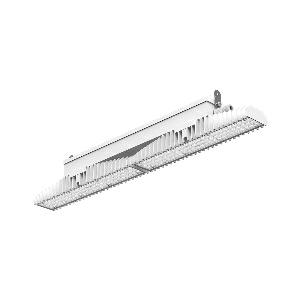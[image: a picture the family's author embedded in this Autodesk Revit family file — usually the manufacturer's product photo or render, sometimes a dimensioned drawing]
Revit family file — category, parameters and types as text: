
# Revit family: 3f_filippi_-_3f_lem_ampio_3f_filippi_-_59161_-_3f_lem_1_1_led_100-865_cr_ampio_7060
name_source: partatom
category: Lighting Fixtures
units: mm (PartAtom-declared; Revit-internal decimal feet)

## family parameters
Cut with Voids When Loaded = No
Host = Face
Light Source = No
Part Type = Normal
Room Calculation Point = No
Round Connector Dimension = Use Diameter
Shared = No

## types (1)
- 3F Filippi - 3F LEM Ampio (1 x LED, 16989 lm, 109 W, 6500 K)
    Apparent Load = 109 VA
    Approval mark = CE
    CIE Flux Codes = 60 92 99 100 100
    Color Rendering = 80
    Color Temperature = 6500 K
    Control Gear = Electronic ballast
    Default Elevation = 1800 mm
    Description = Industrial luminaire with high light output and high luminous efficiency designed with the most innovative technologies for environments with temperature up to 55°C.

ILLUMINOTECHNICAL
Luminous efficiency 100% (DLOR 100%, ULOR 0%).
Initial luminous flux of the luminaire 16989 lm.
Direct symmetric wide distribution: the illuminated area has a rectangular shape.
Installation Interdistance Transv.D = 1.58 x hu - Long.D = 1.45 x hu.
Tabular UGR (CIE 117 - 4H-8H; S=0.25H; 70/50/20): RUG 26.3 - 27.3.
Beam angle: 93° - 99°.
Luminous efficacy 156 lm/W.
Lifetime (L93/B10): 30000 h. (tq+25°C)
Lifetime (L90/B10): 50000 h. (tq+25°C)
Lifetime (L85/B10): 80000 h. (tq+25°C)
Lifetime (L80/B10): 100000 h. (tq+25°C)
Lifetime (L85/B10): 50000 h. (tq+55°C)
Sudden decreased luminous flux after 50000 hours: 0% (C0).
Photobiological safety in compliance with IEC/TR 62778: RG0 risk exempt, (IEC 62471).
In compliance with IEC/EN 62722-2-1 - IEC/EN 62717 standards.

SOURCE
2 Mid-Power linear LED modules 50W/865.
Energy efficiency class (UE 2019/2020 - UE 2019/2015): C.
CIE 13.3 Colour rendering index: CRI >80 (R9 <50%).
IES TM-30 Fidelity Index: Rf = 84 Rg = 95.
CCT nominal colour temperature 6500 K.
Colour initial tolerance (MacAdam): SDCM 3.

MECHANICAL
Passive modular heatsinks in die-casted aluminium, painted in white colour.
To optimize the thermal management of the LED module, the heatsinks are oversized and provided with self-cleaning of cooling fins.
Wiring body in aluminium and galvanised steel anchored solidly to the sinks and thermally separated.
3F Lens lenses with high luminous efficiency, transparent methacrylate (PMMA), fixed to the LED modules.
Fixing brackets in stainless steel.
Luminaire with limited surface temperature. - D - (EN 60598-2-24)
Dimensions: 1099x115 mm, height 150 mm. Weight 10.47 kg.
IP65 protection degree.
Mechanical strength to impacts IK06 (1 joule).
Glow-wire test resistance 650°C.

ELECTRICAL
Halogen Free electronic wiring 230V-50/60Hz, power factor 0.97, THD <25%, constant output current, class I, 1 driver.
Power of the luminaire 109 W.
ENEC - CE.
SAFE FLICKER: PstLM=<1 and SVM=<0.4 (IEC TR 61547-1 and IEC TR 63158), to ensure a more comfortable and safe light.
Luminaire compliant with EN 60598-2-22 for power supply from a centralised emergency system CPSS (Central Power Supply System), not incorporated in the luminaire - high risk areas excluded. The default power and flux are 100% in AC and 100% in DC.
Ambient temperature from -30°C to +55°C.
Temperature class T6 max 85°C.
Quick connection via M20 3P connector with 9-13 mm tightening range.
Power unit positioned on a separate compartment by the LED module to ensure optimum temperatures of cabling components, to be inspectable and maintainable.
Relative humidity UR: <85%.

INSTALLATION
Ceiling / Suspended / Wall.
All accessories dedicated to this product are available on the Catalog and on our website www.3F-Filippi.com.

APPLICATIONS
In commercial environments, exhibition and industrial areas, stores, open areas.
Applications with high ambient temperature up to 55°C.
Environments in which it is necessary a total protection against falling fragments (eg environments with foodstuffs or machines with moving parts or with extreme temperature changes), use luminaires with polycarbonate lenses.

WARNING
Fixture not suitable for cold stores with an ambient temperature <0°C and/or relative humidity >85%.
Luminaire designed for disposal/recycling at end-of-life.
Replaceable (LED only) light source by a professional. Replaceable control gear by a professional.
    Height = 150 mm
    Lamp = 1 x LED
    Lamp Light Flux = 16989 lm
    Lamp Power = 109 W
    Lamp count = 1
    Length = 1099 mm
    Lifetime = 50000 h
    Luminous efficacy = 156 lm/W
    Manufacturer = 3F Filippi
    ModVariant = No
    Model = 3F Filippi - 59161 - 3F LEM 1+1 LED 100-865 CR AMPIO
    Mounting Place = Ceiling
    Mounting Type = Pendant
    Number of Poles = 1
    OnlyDefault = Yes
    Power Factor = 1
    Product Name = 3F Filippi - 3F LEM Ampio
    Product group = pendant luminaire
    ProductGroupID = 9
    Protection Class = Protection class I
    Protection Degree = IP 65
    RLX_Detail_Level = 1
    RLX_Emergency_Light_Flux = 0 lm
    RLX_Emergency_Type = 0
    RLX_Emergency_Type_DB = No
    RlxData = <blob elided: 83649 chars, md5=13ef259e>
    Socket = socket
    Standby Power = 0 W
    System Light Flux = 16989 lm
    System Power = 109 W
    Type Comments = Product without accessories
    Type Image = 3f_filippi_-_lem_11.jpg
    URL = http://relux.com
    VarID = ---
    Voltage = 0 V
    Weight = 0.00 kg
    Width = 115 mm

## geometry (parser evidence)
native form markers: Blend x4, Sweep x13
no freeform markers — native parametric forms only
